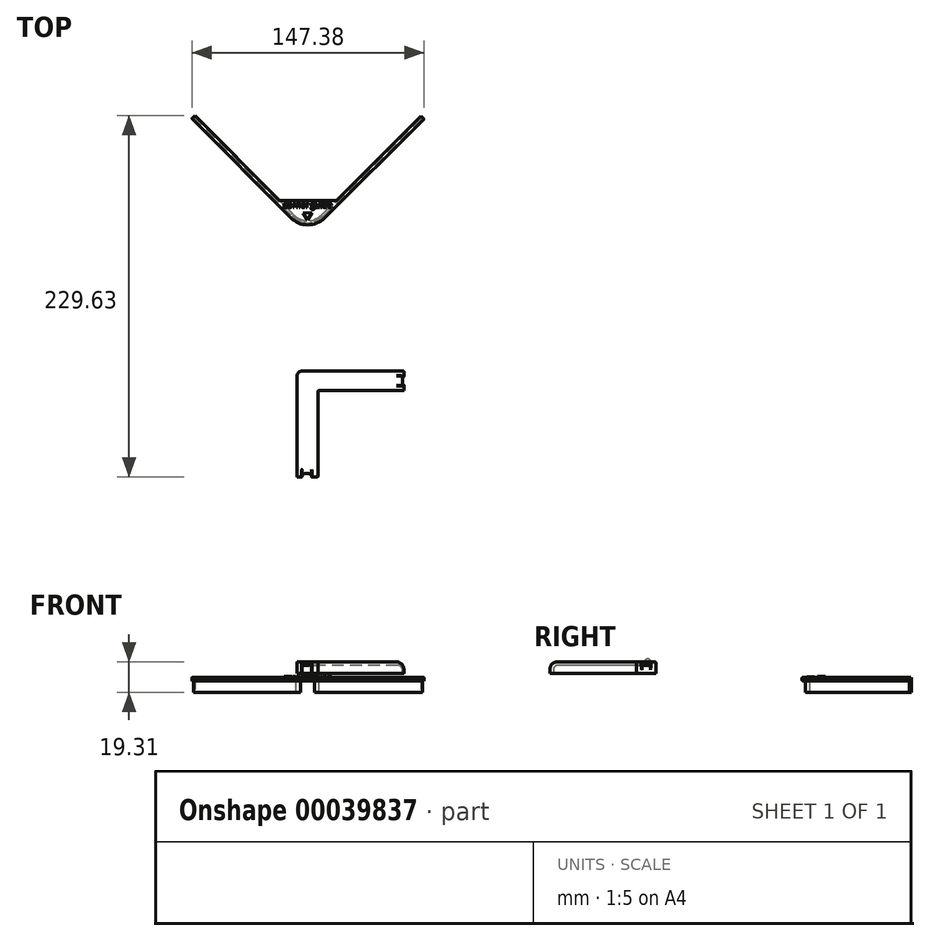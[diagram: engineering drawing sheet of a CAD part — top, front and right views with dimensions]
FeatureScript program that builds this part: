
annotation { "Feature Type Name" : "Feature", "Feature Type Description" : "" }
export const myFeature = defineFeature(function(context is Context, id is Id, definition is map)
    precondition{}
    {
        {
            var Q0;
            Q0=qCreatedBy(makeId("Top.planeOp"),FACE);
            var sketch = newSketch(context, id + "F30", { "sketchPlane" : qUnion([Q0])});
            skLineSegment(sketch, "E0", {"start": v(-39.1, 89.97) * mm, "end": v(-39.1, 1.07) * mm});
            skLineSegment(sketch, "E1", {"start": v(-26.4, -11.63) * mm, "end": v(62.5, -11.63) * mm});
            skLineSegment(sketch, "E2.rect.bottom", {"start": v(-13.7, 13.77) * mm, "end": v(-64.5, 13.77) * mm, "construction": true});
            skLineSegment(sketch, "E2.rect.left", {"start": v(-13.7, 13.77) * mm, "end": v(-13.7, -37.03) * mm, "construction": true});
            skPoint(sketch, "E2.rect.middle", {"position": v(-39.1, -11.63) * mm});
            skArc(sketch, "E3.filletArc", {"start": v(-39.1, 1.07) * mm, "mid": v(-35.39, -7.91) * mm, "end": v(-26.4, -11.63) * mm});
            skSolve(sketch);
        }
        {
            var Q0;
            Q0=qCreatedBy(makeId("Right.planeOp"),FACE);
            cPlane(context, id + "F0", {"entities" : qUnion([Q0]), "cplaneType" : CPlaneType.OFFSET, "offset" : 60.96 * mm, "width" : 152.4 * mm, "height" : 152.4 * mm});
        }
        {
            var Q0;
            Q0=qCreatedBy(makeId("Top.planeOp"),FACE);
            var sketch = newSketch(context, id + "F1", { "sketchPlane" : qUnion([Q0])});
            skLineSegment(sketch, "E4", {"start": v(-39.15, 13.9) * mm, "end": v(-13.72, -11.53) * mm});
            skPoint(sketch, "E5.visualSharp", {"position": v(-39.15, -11.53) * mm});
            skLineSegment(sketch, "E6", {"start": v(-39.15, 13.9) * mm, "end": v(-39.91, 13.9) * mm});
            skLineSegment(sketch, "E7", {"start": v(-39.91, 13.9) * mm, "end": v(-39.91, 0.28) * mm});
            skLineSegment(sketch, "E8", {"start": v(-27.21, -12.42) * mm, "end": v(-13.72, -12.42) * mm});
            skLineSegment(sketch, "E9", {"start": v(-13.72, -12.42) * mm, "end": v(-13.72, -11.53) * mm});
            skPoint(sketch, "E10.visualSharp", {"position": v(-39.91, -12.42) * mm});
            skArc(sketch, "E10.filletArc", {"start": v(-39.91, 0.28) * mm, "mid": v(-36.2, -8.7) * mm, "end": v(-27.21, -12.42) * mm});
            skSolve(sketch);
        }
        {
            var Q0;
            Q0=qCreatedBy(id+"F0.planeOp",FACE);
            var sketch = newSketch(context, id + "F2", { "sketchPlane" : qUnion([Q0])});
            skLineSegment(sketch, "E11", {"start": v(-11.63, 0) * mm, "end": v(-11.63, -9.53) * mm});
            skLineSegment(sketch, "E12", {"start": v(-11.63, -9.53) * mm, "end": v(-12.9, -9.53) * mm});
            skLineSegment(sketch, "E13", {"start": v(-12.9, -9.53) * mm, "end": v(-12.9, -2.62) * mm});
            skLineSegment(sketch, "E14", {"start": v(-13.33, -2.2) * mm, "end": v(-13.82, -2.2) * mm});
            skLineSegment(sketch, "E15", {"start": v(-14.25, -1.76) * mm, "end": v(-14.25, -0.43) * mm});
            skLineSegment(sketch, "E16", {"start": v(-13.82, 0) * mm, "end": v(-11.63, 0) * mm});
            skPoint(sketch, "E17.visualSharp", {"position": v(-14.25, -2.2) * mm});
            skArc(sketch, "E17.filletArc", {"start": v(-14.25, -1.76) * mm, "mid": v(-14.13, -2.07) * mm, "end": v(-13.82, -2.2) * mm});
            skPoint(sketch, "E18.visualSharp", {"position": v(-14.25, 0) * mm});
            skArc(sketch, "E18.filletArc", {"start": v(-13.82, 0) * mm, "mid": v(-14.13, -0.13) * mm, "end": v(-14.25, -0.43) * mm});
            skPoint(sketch, "E19.visualSharp", {"position": v(-12.9, -2.2) * mm});
            skArc(sketch, "E19.filletArc", {"start": v(-12.9, -2.62) * mm, "mid": v(-13.03, -2.32) * mm, "end": v(-13.33, -2.2) * mm});
            skSolve(sketch);
        }
        {
            var Q0;
            Q0=makeQuery(id+"F2.imprint","IMPRINT",FACE,{"disambiguationData":[TD([[makeQuery(id+"F2.imprint","IMPRINT",EDGE,{"derivedFrom":sQuery(id+"F2.wireOp",EDGE,"E11")}),-1.0]])]});
            var Q1;
            Q1=sQuery(id+"F30.wireOp",EDGE,"E1");
            var Q2;
            Q2=sQuery(id+"F30.wireOp",EDGE,"E3.filletArc");
            var Q3;
            Q3=sQuery(id+"F30.wireOp",EDGE,"E0");
            sweep(context, id + "F3", {"profiles" : qUnion([Q0]), "path" : qUnion([Q1, Q2, Q3])});
        }
        {
            var Q0;
            Q0=makeQuery(id+"F1.imprint","IMPRINT",FACE,{"disambiguationData":[TD([[makeQuery(id+"F1.imprint","IMPRINT",EDGE,{"derivedFrom":sQuery(id+"F1.wireOp",EDGE,"E4")}),-1.0]])]});
            extrude(context, id + "F4", {"entities" : qUnion([Q0]), "operationType" : NewBodyOperationType.ADD, "oppositeDirection" : true, "depth" : 1.27 * mm});
        }
        {
            var Q0;
            Q0=qCreatedBy(makeId("Top.planeOp"),FACE);
            cPlane(context, id + "F5", {"entities" : qUnion([Q0]), "cplaneType" : CPlaneType.OFFSET, "offset" : 10.16 * mm, "oppositeDirection" : true, "width" : 152.4 * mm, "height" : 152.4 * mm});
        }
        {
            var Q0;
            Q0=qCreatedBy(id+"F5.planeOp",FACE);
            var sketch = newSketch(context, id + "F6", { "sketchPlane" : qUnion([Q0])});
            skLineSegment(sketch, "E20.bottom", {"start": v(-38.96, -11.41) * mm, "end": v(-3.91, -11.41) * mm});
            skLineSegment(sketch, "E20.top", {"start": v(-38.96, 13.33) * mm, "end": v(-3.91, 13.33) * mm});
            skLineSegment(sketch, "E20.left", {"start": v(-38.96, -11.41) * mm, "end": v(-38.96, 13.33) * mm});
            skLineSegment(sketch, "E20.right", {"start": v(-3.91, -11.41) * mm, "end": v(-3.91, 13.33) * mm});
            skSolve(sketch);
        }
        {
            var Q0;
            Q0=makeQuery(id+"F6.imprint","IMPRINT",FACE,{"disambiguationData":[TD([[makeQuery(id+"F6.imprint","IMPRINT",EDGE,{"derivedFrom":sQuery(id+"F6.wireOp",EDGE,"E20.bottom")}),1.0]])]});
            extrude(context, id + "F7", {"entities" : qUnion([Q0]), "operationType" : NewBodyOperationType.REMOVE, "depth" : 7.87 * mm});
        }
        {
            var Q0;
            Q0=qCreatedBy(makeId("Top.planeOp"),FACE);
            cPlane(context, id + "F8", {"entities" : qUnion([Q0]), "cplaneType" : CPlaneType.OFFSET, "offset" : 0 * mm, "width" : 152.4 * mm, "height" : 152.4 * mm});
        }
        {
            var Q0;
            Q0=qCreatedBy(makeId("Right.planeOp"),FACE);
            var sketch = newSketch(context, id + "F9", { "sketchPlane" : qUnion([Q0])});
            skLineSegment(sketch, "E21", {"start": v(0, 23.34) * mm, "end": v(0, -29.25) * mm});
            skSolve(sketch);
        }
        {
            var Q0;
            Q0=makeQuery(id+"F3.opSweep","SWEPT_BODY",BODY,{"disambiguationData":[OSD([sQuery(id+"F30.wireOp",EDGE,"E0"),sQuery(id+"F2.wireOp",EDGE,"E11"),sQuery(id+"F2.wireOp",EDGE,"E12"),sQuery(id+"F2.wireOp",EDGE,"E13"),sQuery(id+"F2.wireOp",EDGE,"E14"),sQuery(id+"F2.wireOp",EDGE,"E15"),sQuery(id+"F2.wireOp",EDGE,"E16"),sQuery(id+"F2.wireOp",EDGE,"E17.filletArc"),sQuery(id+"F2.wireOp",EDGE,"E18.filletArc"),sQuery(id+"F2.wireOp",EDGE,"E19.filletArc")])]});
            var Q1;
            Q1=sQuery(id+"F9.wireOp",EDGE,"E21");
            transform(context, id + "F10", {"entities" : qUnion([Q0]), "transformType" : TransformType.ROTATION, "transformAxis" : qUnion([Q1]), "angle" : 44.8 * degree, "oppositeDirection" : true, "makeCopy" : false});
        }
        {
            var Q0;
            Q0=qCreatedBy(id+"F8.planeOp",FACE);
            var sketch = newSketch(context, id + "F11", { "sketchPlane" : qUnion([Q0])});
            skText(sketch, "E22", { "text": "corner guide", "fontName": "OpenSans-Bold.ttf"});
            const initialGuessF11  = {"E22": [-0.03477, -0.02219, 1, 0, 0.0035]};
            skSetInitialGuess(sketch, initialGuessF11);
            skSolve(sketch);
        }
        {
            var Q0;
            Q0 = qSketchRegion(id + "F11", true);
            extrude(context, id + "F12", {"entities" : qUnion([Q0]), "operationType" : NewBodyOperationType.ADD, "depth" : 0.5 * mm});
        }
        {
            var Q0;
            Q0=qCreatedBy(id+"F8.planeOp",FACE);
            var sketch = newSketch(context, id + "F13", { "sketchPlane" : qUnion([Q0])});
            skCircle(sketch, "E23.cCircle", {"center": v(-19.58, -27.09) * mm, "radius": 1.56 * mm, "construction": true});
            skLineSegment(sketch, "E23.0", {"start": v(-22.3, -25.55) * mm, "end": v(-16.89, -25.5) * mm});
            skLineSegment(sketch, "E23.1", {"start": v(-16.89, -25.5) * mm, "end": v(-19.56, -30.22) * mm});
            skLineSegment(sketch, "E23.2", {"start": v(-19.56, -30.22) * mm, "end": v(-22.3, -25.55) * mm});
            skPoint(sketch, "E23.0.midPoint", {"position": v(-19.6, -25.53) * mm});
            skSolve(sketch);
        }
        {
            var Q0;
            Q0=makeQuery(id+"F13.imprint","IMPRINT",FACE,{"disambiguationData":[TD([[makeQuery(id+"F13.imprint","IMPRINT",EDGE,{"derivedFrom":sQuery(id+"F13.wireOp",EDGE,"E23.0")}),-1.0]])]});
            extrude(context, id + "F14", {"entities" : qUnion([Q0]), "operationType" : NewBodyOperationType.ADD, "depth" : 0.25 * mm});
        }
        {
            var Q0;
            Q0=qCreatedBy(makeId("Front.planeOp"),FACE);
            cPlane(context, id + "F15", {"entities" : qUnion([Q0]), "cplaneType" : CPlaneType.OFFSET, "offset" : 152.4 * mm, "width" : 152.4 * mm, "height" : 152.4 * mm});
        }
        {
            var Q0;
            Q0=qCreatedBy(makeId("Top.planeOp"),FACE);
            var sketch = newSketch(context, id + "F16", { "sketchPlane" : qUnion([Q0])});
            skLineSegment(sketch, "E24.bottom", {"start": v(45.12, -129.22) * mm, "end": v(40.7, -129.22) * mm});
            skLineSegment(sketch, "E24.top", {"start": v(45.12, -135.38) * mm, "end": v(40.7, -135.38) * mm});
            skLineSegment(sketch, "E24.left", {"start": v(45.12, -129.22) * mm, "end": v(45.12, -135.38) * mm});
            skLineSegment(sketch, "E24.right", {"start": v(40.7, -129.22) * mm, "end": v(40.7, -135.38) * mm});
            skSolve(sketch);
        }
        {
            var Q0;
            Q0=qCreatedBy(makeId("Top.planeOp"),FACE);
            cPlane(context, id + "F17", {"entities" : qUnion([Q0]), "cplaneType" : CPlaneType.OFFSET, "offset" : 7.62 * mm, "width" : 152.4 * mm, "height" : 152.4 * mm});
        }
        {
            var Q0;
            Q0=qCreatedBy(id+"F15.planeOp",FACE);
            var sketch = newSketch(context, id + "F18", { "sketchPlane" : qUnion([Q0])});
            skLineSegment(sketch, "E25", {"start": v(40.7, 0) * mm, "end": v(40.7, 4.83) * mm});
            skLineSegment(sketch, "E26", {"start": v(37.91, 7.62) * mm, "end": v(0, 7.62) * mm});
            skPoint(sketch, "E27.visualSharp", {"position": v(40.7, 7.62) * mm});
            skArc(sketch, "E27.filletArc", {"start": v(40.7, 4.83) * mm, "mid": v(39.89, 6.8) * mm, "end": v(37.91, 7.62) * mm});
            skSolve(sketch);
        }
        {
            var Q0;
            Q0=qCreatedBy(id+"F15.planeOp",FACE);
            cPlane(context, id + "F19", {"entities" : qUnion([Q0]), "cplaneType" : CPlaneType.OFFSET, "offset" : 31.75 * mm, "width" : 152.4 * mm, "height" : 152.4 * mm});
        }
        {
            var Q0;
            Q0=qCreatedBy(id+"F17.planeOp",FACE);
            var sketch = newSketch(context, id + "F20", { "sketchPlane" : qUnion([Q0])});
            skLineSegment(sketch, "E28", {"start": v(0, -152.4) * mm, "end": v(0, -184.15) * mm});
            skSolve(sketch);
        }
        {
            var Q0;
            Q0=qCreatedBy(makeId("Right.planeOp"),FACE);
            var sketch = newSketch(context, id + "F21", { "sketchPlane" : qUnion([Q0])});
            skLineSegment(sketch, "E29", {"start": v(-184.15, 7.62) * mm, "end": v(-188.42, 7.62) * mm});
            skLineSegment(sketch, "E30", {"start": v(-191.21, 4.83) * mm, "end": v(-191.21, 0) * mm});
            skPoint(sketch, "E31.visualSharp", {"position": v(-191.21, 7.62) * mm});
            skArc(sketch, "E31.filletArc", {"start": v(-188.42, 7.62) * mm, "mid": v(-190.4, 6.8) * mm, "end": v(-191.21, 4.83) * mm});
            skSolve(sketch);
        }
        {
            var Q0;
            Q0=makeQuery(id+"F16.imprint","IMPRINT",FACE,{"disambiguationData":[TD([[makeQuery(id+"F16.imprint","IMPRINT",EDGE,{"derivedFrom":sQuery(id+"F16.wireOp",EDGE,"E24.bottom")}),1.0]])]});
            var Q1;
            Q1=sQuery(id+"F18.wireOp",EDGE,"E25");
            var Q2;
            Q2=sQuery(id+"F18.wireOp",EDGE,"E27.filletArc");
            var Q3;
            Q3=sQuery(id+"F18.wireOp",EDGE,"E26");
            var Q4;
            Q4=sQuery(id+"F20.wireOp",EDGE,"E28");
            var Q5;
            Q5=sQuery(id+"F21.wireOp",EDGE,"E29");
            var Q6;
            Q6=sQuery(id+"F21.wireOp",EDGE,"E31.filletArc");
            var Q7;
            Q7=sQuery(id+"F21.wireOp",EDGE,"E30");
            sweep(context, id + "F22", {"profiles" : qUnion([Q0]), "path" : qUnion([Q1, Q2, Q3, Q4, Q5, Q6, Q7])});
        }
        {
            var Q0;
            Q0=qCreatedBy(id+"F17.planeOp",FACE);
            var sketch = newSketch(context, id + "F23", { "sketchPlane" : qUnion([Q0])});
            skLineSegment(sketch, "E32", {"start": v(-23.38, -126.14) * mm, "end": v(41.6, -126.14) * mm});
            skLineSegment(sketch, "E33", {"start": v(41.6, -126.14) * mm, "end": v(41.6, -138.53) * mm});
            skLineSegment(sketch, "E34", {"start": v(41.6, -138.53) * mm, "end": v(-12.53, -138.53) * mm});
            skLineSegment(sketch, "E35", {"start": v(-13.04, -139.04) * mm, "end": v(-13.04, -193.35) * mm});
            skLineSegment(sketch, "E36", {"start": v(-13.04, -193.35) * mm, "end": v(-26.18, -193.35) * mm});
            skLineSegment(sketch, "E37", {"start": v(-26.18, -193.35) * mm, "end": v(-26.18, -128.93) * mm});
            skPoint(sketch, "E38.visualSharp", {"position": v(-26.18, -126.14) * mm});
            skArc(sketch, "E38.filletArc", {"start": v(-23.38, -126.14) * mm, "mid": v(-25.36, -126.95) * mm, "end": v(-26.18, -128.93) * mm});
            skPoint(sketch, "E39.visualSharp", {"position": v(-13.04, -138.53) * mm});
            skArc(sketch, "E39.filletArc", {"start": v(-12.53, -138.53) * mm, "mid": v(-12.89, -138.68) * mm, "end": v(-13.04, -139.04) * mm});
            skSolve(sketch);
        }
        {
            var Q0;
            Q0=makeQuery(id+"F22.opSweep","MID_CAP_EDGE",EDGE,{"disambiguationData":[OSD([sQuery(id+"F16.wireOp",EDGE,"E24.bottom"),sQuery(id+"F20.wireOp",VERTEX,"E28.start")])],"capPos":3.0});
            var Q1;
            Q1=makeQuery(id+"F22.opSweep","MID_CAP_EDGE",EDGE,{"disambiguationData":[OSD([sQuery(id+"F16.wireOp",EDGE,"E24.top"),sQuery(id+"F20.wireOp",VERTEX,"E28.start")])],"capPos":3.0});
            fillet(context, id + "F24", {"entities" : qUnion([Q0, Q1]), "radius" : 3.05 * mm, "tangentPropagation" : true, "allowEdgeOverflow" : false});
        }
        {
            var Q0;
            Q0=makeQuery(id+"F22.opSweep","SWEPT_EDGE",EDGE,{"disambiguationData":[OSD([sQuery(id+"F16.wireOp",EDGE,"E24.bottom"),sQuery(id+"F16.wireOp",EDGE,"E24.right"),sQuery(id+"F21.wireOp",EDGE,"E30")])]});
            var Q1;
            Q1=makeQuery(id+"F22.opSweep","SWEPT_EDGE",EDGE,{"disambiguationData":[OSD([sQuery(id+"F16.wireOp",EDGE,"E24.top"),sQuery(id+"F16.wireOp",EDGE,"E24.right"),sQuery(id+"F21.wireOp",EDGE,"E30")])]});
            fillet(context, id + "F25", {"entities" : qUnion([Q0, Q1]), "radius" : 2.03 * mm, "tangentPropagation" : true, "allowEdgeOverflow" : false});
        }
        {
            var Q0;
            Q0=makeQuery(id+"F23.imprint","IMPRINT",FACE,{"disambiguationData":[TD([[makeQuery(id+"F23.imprint","IMPRINT",EDGE,{"derivedFrom":sQuery(id+"F23.wireOp",EDGE,"E32")}),-1.0]])]});
            extrude(context, id + "F26", {"entities" : qUnion([Q0]), "depth" : 2.16 * mm, "hasSecondDirection" : true, "secondDirectionOppositeDirection" : true, "secondDirectionDepth" : 5.08 * mm});
        }
        {
            var Q0;
            Q0=makeQuery(id+"F22.opSweep","SWEPT_BODY",BODY,{"disambiguationData":[OSD([sQuery(id+"F16.wireOp",EDGE,"E24.bottom"),sQuery(id+"F16.wireOp",EDGE,"E24.top"),sQuery(id+"F16.wireOp",EDGE,"E24.left"),sQuery(id+"F16.wireOp",EDGE,"E24.right"),sQuery(id+"F21.wireOp",EDGE,"E30")])]});
            var Q1;
            Q1=makeQuery(id+"F26.opExtrude","SWEPT_BODY",BODY,{"disambiguationData":[OSD([sQuery(id+"F23.wireOp",EDGE,"E32"),sQuery(id+"F23.wireOp",EDGE,"E33"),sQuery(id+"F23.wireOp",EDGE,"E34"),sQuery(id+"F23.wireOp",EDGE,"E35"),sQuery(id+"F23.wireOp",EDGE,"E36"),sQuery(id+"F23.wireOp",EDGE,"E37"),sQuery(id+"F23.wireOp",EDGE,"E38.filletArc"),sQuery(id+"F23.wireOp",EDGE,"E39.filletArc")])]});
            booleanBodies(context, id + "F27", {"operationType" : BooleanOperationType.SUBTRACTION, "tools" : qUnion([Q0]), "targets" : qUnion([Q1])});
        }
        {
            var Q0;
            {var subQ0=sQuery(id+"F23.wireOp",EDGE,"E36");var subQ1=sQuery(id+"F23.wireOp",EDGE,"E35");Q0=makeQuery(id+"F27.opBoolean","SPLIT",EDGE,{"disambiguationData":[TD([makeQuery(id+"F26.opExtrude","SWEPT_FACE",FACE,{"disambiguationData":[OSD([subQ1])]})])],"derivedFrom":makeQuery(id+"F26.opExtrude","CAP_EDGE",EDGE,{"disambiguationData":[OSD([subQ0])],"isStart":false})});}
            var Q1;
            {var subQ0=sQuery(id+"F23.wireOp",EDGE,"E37");var subQ1=sQuery(id+"F23.wireOp",EDGE,"E36");Q1=makeQuery(id+"F27.opBoolean","SPLIT",EDGE,{"disambiguationData":[TD([makeQuery(id+"F26.opExtrude","SWEPT_FACE",FACE,{"disambiguationData":[OSD([subQ0])]})])],"derivedFrom":makeQuery(id+"F26.opExtrude","CAP_EDGE",EDGE,{"disambiguationData":[OSD([subQ1])],"isStart":false})});}
            var Q2;
            {var subQ0=sQuery(id+"F23.wireOp",EDGE,"E32");var subQ1=sQuery(id+"F23.wireOp",EDGE,"E33");Q2=makeQuery(id+"F27.opBoolean","SPLIT",EDGE,{"disambiguationData":[TD([makeQuery(id+"F26.opExtrude","SWEPT_FACE",FACE,{"disambiguationData":[OSD([subQ0])]})])],"derivedFrom":makeQuery(id+"F26.opExtrude","CAP_EDGE",EDGE,{"disambiguationData":[OSD([subQ1])],"isStart":false})});}
            var Q3;
            {var subQ0=sQuery(id+"F23.wireOp",EDGE,"E34");var subQ1=sQuery(id+"F23.wireOp",EDGE,"E33");Q3=makeQuery(id+"F27.opBoolean","SPLIT",EDGE,{"disambiguationData":[TD([makeQuery(id+"F26.opExtrude","SWEPT_FACE",FACE,{"disambiguationData":[OSD([subQ0])]})])],"derivedFrom":makeQuery(id+"F26.opExtrude","CAP_EDGE",EDGE,{"disambiguationData":[OSD([subQ1])],"isStart":false})});}
            fillet(context, id + "F28", {"entities" : qUnion([Q0, Q1, Q2, Q3]), "radius" : 4.57 * mm, "tangentPropagation" : true, "allowEdgeOverflow" : false});
        }
        {
            var Q0;
            {var subQ0=sQuery(id+"F23.wireOp",EDGE,"E37");var subQ1=makeQuery(id+"F26.opExtrude","SWEPT_FACE",FACE,{"disambiguationData":[OSD([subQ0])]});var subQ2=sQuery(id+"F23.wireOp",EDGE,"E36");Q0=makeQuery(id+"F28.opFillet","BLEND_EDGE",EDGE,{"blendedFrom":[makeQuery(id+"F27.opBoolean","SPLIT",EDGE,{"disambiguationData":[TD([subQ1])],"derivedFrom":makeQuery(id+"F26.opExtrude","CAP_EDGE",EDGE,{"disambiguationData":[OSD([subQ2])],"isStart":false})}),subQ1],"blendedInto":[subQ1]});}
            var Q1;
            {var subQ0=sQuery(id+"F23.wireOp",EDGE,"E35");var subQ1=makeQuery(id+"F26.opExtrude","SWEPT_FACE",FACE,{"disambiguationData":[OSD([subQ0])]});var subQ2=sQuery(id+"F23.wireOp",EDGE,"E36");Q1=makeQuery(id+"F28.opFillet","BLEND_EDGE",EDGE,{"blendedFrom":[makeQuery(id+"F27.opBoolean","SPLIT",EDGE,{"disambiguationData":[TD([subQ1])],"derivedFrom":makeQuery(id+"F26.opExtrude","CAP_EDGE",EDGE,{"disambiguationData":[OSD([subQ2])],"isStart":false})}),subQ1],"blendedInto":[subQ1]});}
            var Q2;
            Q2=makeQuery(id+"F27.opBoolean","INTERSECT",EDGE,{"derivedFrom":[makeQuery(id+"F22.opSweep","SWEPT_FACE",FACE,{"disambiguationData":[OSD([sQuery(id+"F16.wireOp",EDGE,"E24.bottom"),sQuery(id+"F21.wireOp",EDGE,"E30")])]}),makeQuery(id+"F26.opExtrude","CAP_FACE",FACE,{"disambiguationData":[OSD([sQuery(id+"F23.wireOp",EDGE,"E32"),sQuery(id+"F23.wireOp",EDGE,"E33"),sQuery(id+"F23.wireOp",EDGE,"E34"),sQuery(id+"F23.wireOp",EDGE,"E35"),sQuery(id+"F23.wireOp",EDGE,"E36"),sQuery(id+"F23.wireOp",EDGE,"E37"),sQuery(id+"F23.wireOp",EDGE,"E38.filletArc"),sQuery(id+"F23.wireOp",EDGE,"E39.filletArc")])],"isStart":false})]});
            var Q3;
            Q3=makeQuery(id+"F27.opBoolean","INTERSECT",EDGE,{"derivedFrom":[makeQuery(id+"F22.opSweep","SWEPT_FACE",FACE,{"disambiguationData":[OSD([sQuery(id+"F16.wireOp",EDGE,"E24.top"),sQuery(id+"F21.wireOp",EDGE,"E30")])]}),makeQuery(id+"F26.opExtrude","CAP_FACE",FACE,{"disambiguationData":[OSD([sQuery(id+"F23.wireOp",EDGE,"E32"),sQuery(id+"F23.wireOp",EDGE,"E33"),sQuery(id+"F23.wireOp",EDGE,"E34"),sQuery(id+"F23.wireOp",EDGE,"E35"),sQuery(id+"F23.wireOp",EDGE,"E36"),sQuery(id+"F23.wireOp",EDGE,"E37"),sQuery(id+"F23.wireOp",EDGE,"E38.filletArc"),sQuery(id+"F23.wireOp",EDGE,"E39.filletArc")])],"isStart":false})]});
            fillet(context, id + "F29", {"entities" : qUnion([Q0, Q1, Q2, Q3]), "radius" : 0.3 * mm, "tangentPropagation" : true, "allowEdgeOverflow" : false});
        }
    });
